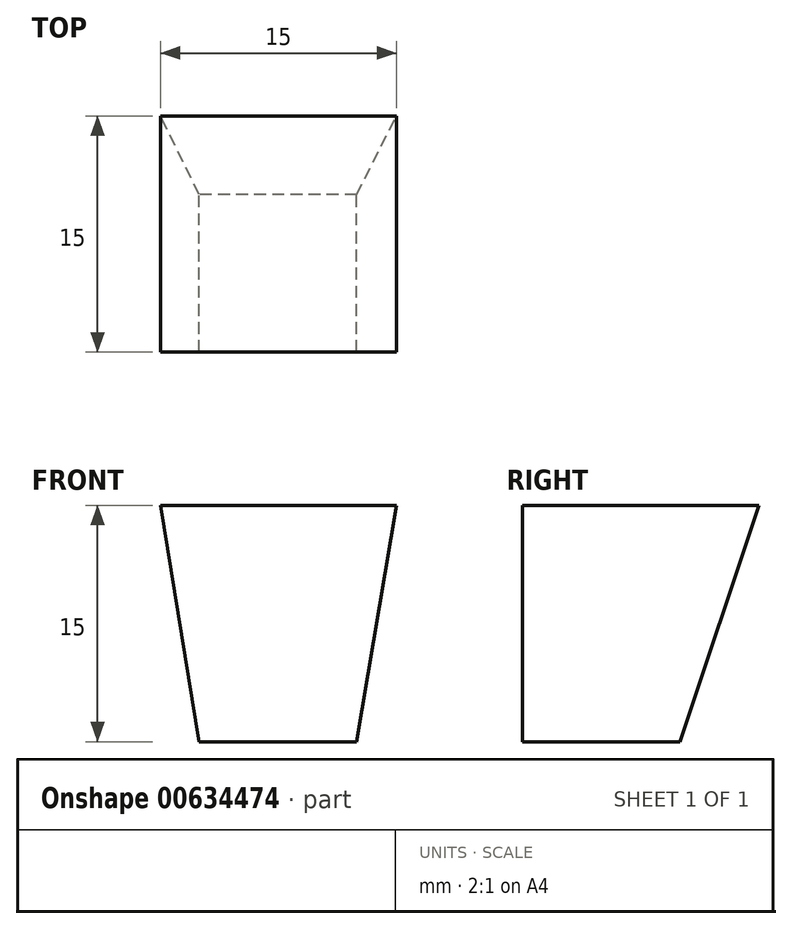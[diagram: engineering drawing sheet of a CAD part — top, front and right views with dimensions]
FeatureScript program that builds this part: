
annotation { "Feature Type Name" : "Feature", "Feature Type Description" : "" }
export const myFeature = defineFeature(function(context is Context, id is Id, definition is map)
    precondition{}
    {
        {
            var Q0;
            Q0=qCreatedBy(makeId("Top.planeOp"),FACE);
            var sketch = newSketch(context, id + "F0", { "sketchPlane" : qUnion([Q0])});
            skLineSegment(sketch, "E0.bottom", {"start": v(0, 0) * mm, "end": v(-10, 0) * mm});
            skLineSegment(sketch, "E0.top", {"start": v(0, 10) * mm, "end": v(-10, 10) * mm});
            skLineSegment(sketch, "E0.left", {"start": v(0, 0) * mm, "end": v(0, 10) * mm});
            skLineSegment(sketch, "E0.right", {"start": v(-10, 0) * mm, "end": v(-10, 10) * mm});
            skSolve(sketch);
        }
        {
            var Q0;
            Q0=qCreatedBy(makeId("Top.planeOp"),FACE);
            cPlane(context, id + "F1", {"entities" : qUnion([Q0]), "cplaneType" : CPlaneType.OFFSET, "offset" : 15 * mm, "width" : 152.4 * mm, "height" : 152.4 * mm});
        }
        {
            var Q0;
            Q0=qCreatedBy(id+"F1.planeOp",FACE);
            var sketch = newSketch(context, id + "F2", { "sketchPlane" : qUnion([Q0])});
            skLineSegment(sketch, "E1.bottom", {"start": v(2.54, 0) * mm, "end": v(-12.46, 0) * mm});
            skLineSegment(sketch, "E1.top", {"start": v(2.54, 15) * mm, "end": v(-12.46, 15) * mm});
            skLineSegment(sketch, "E1.left", {"start": v(2.54, 0) * mm, "end": v(2.54, 15) * mm});
            skLineSegment(sketch, "E1.right", {"start": v(-12.46, 0) * mm, "end": v(-12.46, 15) * mm});
            skSolve(sketch);
        }
        {
            var Q0;
            Q0 = qSketchRegion(id + "F0", true);
            var Q1;
            Q1 = qSketchRegion(id + "F2", true);
            loft(context, id + "F3", {"sheetProfilesArray" : [{ "sheetProfileEntities" : qUnion([Q0]) }, { "sheetProfileEntities" : qUnion([Q1]) }]});
        }
    });
